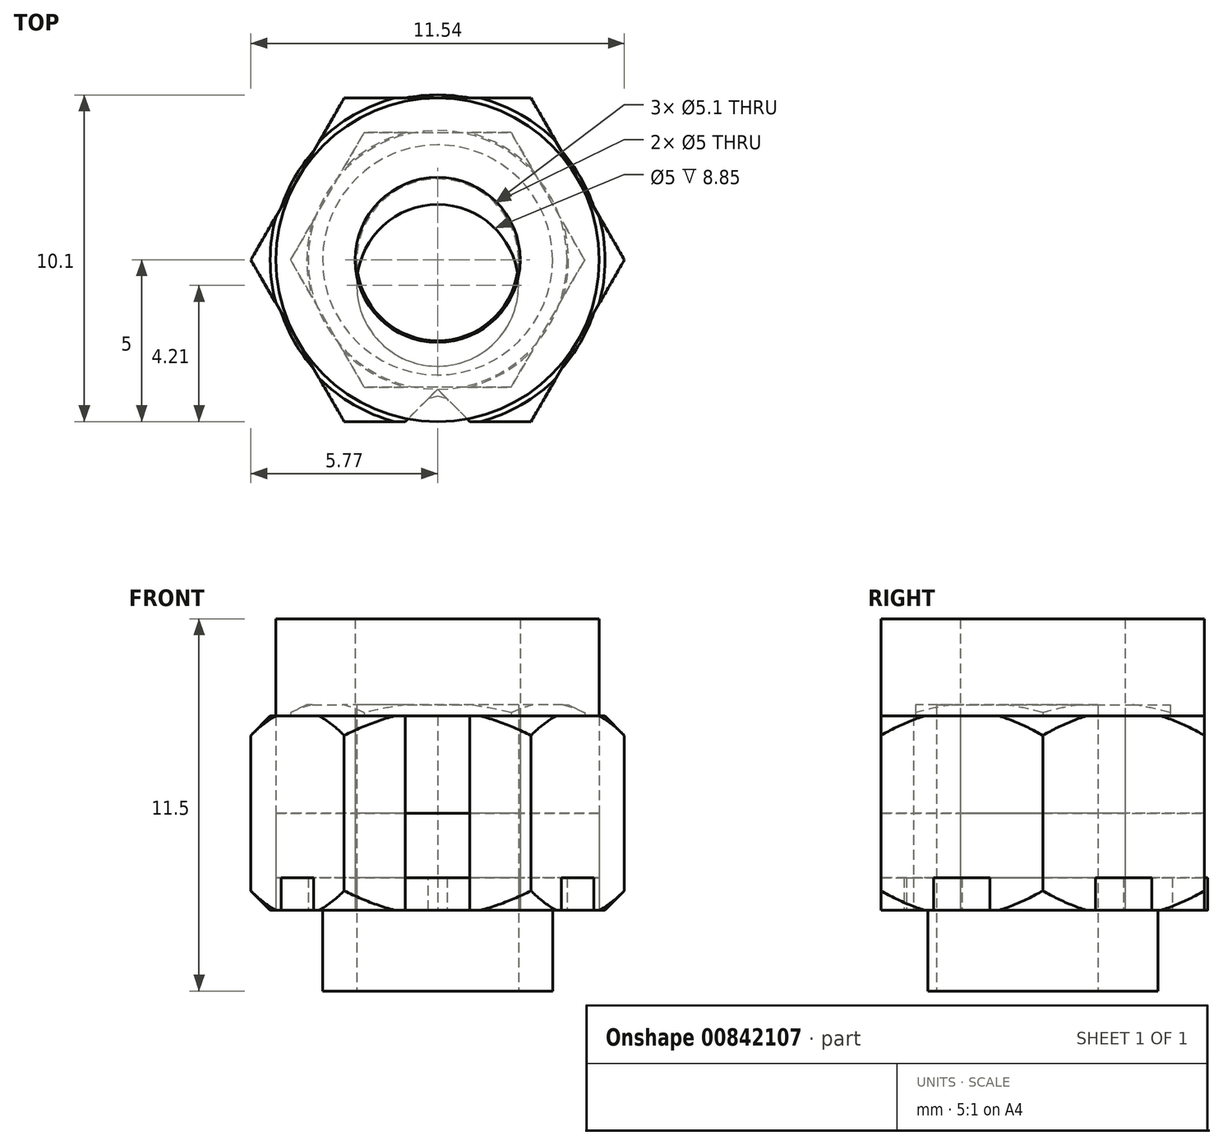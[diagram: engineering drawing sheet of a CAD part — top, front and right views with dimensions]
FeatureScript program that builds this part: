
annotation { "Feature Type Name" : "Feature", "Feature Type Description" : "" }
export const myFeature = defineFeature(function(context is Context, id is Id, definition is map)
    precondition{}
    {
        {
            var Q0;
            Q0=qCreatedBy(makeId("Top.planeOp"),FACE);
            var sketch = newSketch(context, id + "F0", { "sketchPlane" : qUnion([Q0])});
            skArc(sketch, "E0", {"start": v(1.94, -4.72) * mm, "mid": v(0, 5.1) * mm, "end": v(-1.94, -4.72) * mm});
            skCircle(sketch, "E1", {"center": v(0, 0) * mm, "radius": 3.56 * mm});
            skCircle(sketch, "E2", {"center": v(0, -0.79) * mm, "radius": 2.5 * mm});
            skLineSegment(sketch, "E3", {"start": v(-1.94, -4.72) * mm, "end": v(1.94, -4.72) * mm, "construction": true});
            skLineSegment(sketch, "E4", {"start": v(1.94, -4.72) * mm, "end": v(0, -4.22) * mm});
            skLineSegment(sketch, "E5", {"start": v(0, -4.22) * mm, "end": v(-1.94, -4.72) * mm});
            skCircle(sketch, "E6.cCircle", {"center": v(0, 0) * mm, "radius": 3.94 * mm, "construction": true});
            skLineSegment(sketch, "E6.0", {"start": v(-2.27, 3.94) * mm, "end": v(2.27, 3.94) * mm});
            skLineSegment(sketch, "E6.1", {"start": v(2.27, 3.93) * mm, "end": v(4.54, 0) * mm});
            skLineSegment(sketch, "E6.2", {"start": v(4.54, 0) * mm, "end": v(2.27, -3.94) * mm});
            skLineSegment(sketch, "E6.3", {"start": v(2.27, -3.94) * mm, "end": v(-2.27, -3.94) * mm});
            skLineSegment(sketch, "E6.4", {"start": v(-2.27, -3.94) * mm, "end": v(-4.54, 0) * mm});
            skLineSegment(sketch, "E6.5", {"start": v(-4.54, 0) * mm, "end": v(-2.27, 3.94) * mm});
            skPoint(sketch, "E6.0.midPoint", {"position": v(0, 3.94) * mm});
            skSolve(sketch);
        }
        {
            var Q0;
            Q0=makeQuery(id+"F0.imprint","IMPRINT",FACE,{"disambiguationData":[TD([[makeQuery(id+"F0.imprint","IMPRINT",EDGE,{"derivedFrom":sQuery(id+"F0.wireOp",EDGE,"E1")}),-1.0]])]});
            var Q1;
            Q1=makeQuery(id+"F0.imprint","IMPRINT",FACE,{"disambiguationData":[TD([[makeQuery(id+"F0.imprint","IMPRINT",EDGE,{"derivedFrom":sQuery(id+"F0.wireOp",EDGE,"E1")}),1.0]])]});
            extrude(context, id + "F1", {"entities" : qUnion([Q0, Q1]), "depth" : 6.35 * mm, "offsetDistance" : 25 * mm});
        }
        {
            var Q0;
            Q0=makeQuery(id+"F0.imprint","IMPRINT",FACE,{"disambiguationData":[TD([[makeQuery(id+"F0.imprint","IMPRINT",EDGE,{"derivedFrom":sQuery(id+"F0.wireOp",EDGE,"E0")}),1.0]])]});
            extrude(context, id + "F2", {"entities" : qUnion([Q0]), "operationType" : NewBodyOperationType.ADD, "depth" : 1 * mm, "offsetDistance" : 25 * mm});
        }
        {
            var Q0;
            Q0=makeQuery(id+"F0.imprint","IMPRINT",FACE,{"disambiguationData":[TD([[makeQuery(id+"F0.imprint","IMPRINT",EDGE,{"derivedFrom":sQuery(id+"F0.wireOp",EDGE,"E1")}),1.0]])]});
            extrude(context, id + "F3", {"entities" : qUnion([Q0]), "operationType" : NewBodyOperationType.ADD, "oppositeDirection" : true, "depth" : 2.5 * mm, "offsetDistance" : 25 * mm});
        }
        {
            var Q0;
            Q0=qCreatedBy(makeId("Front.planeOp"),FACE);
            var sketch = newSketch(context, id + "F4", { "sketchPlane" : qUnion([Q0])});
            skPoint(sketch, "E7.0", {"position": v(4.54, 6.35) * mm});
            skLineSegment(sketch, "E8", {"start": v(4.54, 6.35) * mm, "end": v(4.54, 6.1) * mm});
            skLineSegment(sketch, "E9", {"start": v(4.54, 6.1) * mm, "end": v(4.04, 6.35) * mm});
            skLineSegment(sketch, "E10", {"start": v(4.04, 6.35) * mm, "end": v(4.54, 6.35) * mm});
            skLineSegment(sketch, "E11", {"start": v(0, 0) * mm, "end": v(0, 6.35) * mm, "construction": true});
            skSolve(sketch);
        }
        {
            var Q0;
            Q0=qSketchRegion(id+"F4",true);
            var Q1;
            Q1=sQuery(id+"F4.wireOp",EDGE,"E11");
            revolve(context, id + "F5", {"operationType" : NewBodyOperationType.REMOVE, "entities" : qUnion([Q0]), "axis" : qUnion([Q1]), "revolveType" : RevolveType.FULL, "oppositeDirection" : true});
        }
        {
            var Q0;
            Q0=qCreatedBy(makeId("Top.planeOp"),FACE);
            var sketch = newSketch(context, id + "F6", { "sketchPlane" : qUnion([Q0])});
            skCircle(sketch, "E12", {"center": v(0, 0) * mm, "radius": 3.56 * mm});
            skCircle(sketch, "E13", {"center": v(0, -0.79) * mm, "radius": 2.5 * mm});
            skCircle(sketch, "E14.cCircle", {"center": v(0, 0) * mm, "radius": 5 * mm, "construction": true});
            skLineSegment(sketch, "E14.0", {"start": v(-2.89, 5) * mm, "end": v(2.89, 5) * mm});
            skLineSegment(sketch, "E14.1", {"start": v(2.89, 5) * mm, "end": v(5.77, 0) * mm});
            skLineSegment(sketch, "E14.2", {"start": v(5.77, 0) * mm, "end": v(2.89, -5) * mm});
            skLineSegment(sketch, "E14.3", {"start": v(2.89, -5) * mm, "end": v(-2.89, -5) * mm});
            skLineSegment(sketch, "E14.4", {"start": v(-2.89, -5) * mm, "end": v(-5.77, 0) * mm});
            skLineSegment(sketch, "E14.5", {"start": v(-5.77, 0) * mm, "end": v(-2.89, 5) * mm});
            skPoint(sketch, "E14.0.midPoint", {"position": v(0, 5) * mm});
            skLineSegment(sketch, "E15", {"start": v(0, -4) * mm, "end": v(-1, -5) * mm});
            skLineSegment(sketch, "E16", {"start": v(1, -5) * mm, "end": v(0, -4) * mm});
            skLineSegment(sketch, "E17", {"start": v(0, 0) * mm, "end": v(0, 1.8) * mm, "construction": true});
            skSolve(sketch);
        }
        {
            var Q0;
            Q0=makeQuery(id+"F6.imprint","IMPRINT",FACE,{"disambiguationData":[TD([[makeQuery(id+"F6.imprint","IMPRINT",EDGE,{"derivedFrom":sQuery(id+"F6.wireOp",EDGE,"E12")}),1.0]])]});
            extrude(context, id + "F7", {"entities" : qUnion([Q0]), "oppositeDirection" : true, "depth" : 2.5 * mm, "offsetDistance" : 25 * mm});
        }
        {
            var Q0;
            Q0=makeQuery(id+"F6.imprint","IMPRINT",FACE,{"disambiguationData":[TD([[makeQuery(id+"F6.imprint","IMPRINT",EDGE,{"derivedFrom":sQuery(id+"F6.wireOp",EDGE,"E12")}),1.0]])]});
            var Q1;
            Q1=makeQuery(id+"F6.imprint","IMPRINT",FACE,{"disambiguationData":[TD([[makeQuery(id+"F6.imprint","IMPRINT",EDGE,{"derivedFrom":sQuery(id+"F6.wireOp",EDGE,"E12")}),-1.0]])]});
            extrude(context, id + "F8", {"entities" : qUnion([Q0, Q1]), "operationType" : NewBodyOperationType.ADD, "depth" : 6 * mm, "offsetDistance" : 25 * mm});
        }
        {
            var Q0;
            Q0=qCreatedBy(makeId("Front.planeOp"),FACE);
            var sketch = newSketch(context, id + "F9", { "sketchPlane" : qUnion([Q0])});
            skPoint(sketch, "E18.0", {"position": v(-5.77, 6) * mm});
            skLineSegment(sketch, "E19", {"start": v(-5.77, 6) * mm, "end": v(-5.77, 5.4) * mm});
            skLineSegment(sketch, "E20", {"start": v(-5.77, 6) * mm, "end": v(-5.17, 6) * mm});
            skLineSegment(sketch, "E21", {"start": v(-5.77, 5.4) * mm, "end": v(-5.17, 6) * mm});
            skLineSegment(sketch, "E22", {"start": v(0, 0) * mm, "end": v(0, 2) * mm, "construction": true});
            skPoint(sketch, "E23.0", {"position": v(-5.77, 3) * mm});
            skLineSegment(sketch, "E24", {"start": v(-5.77, 3) * mm, "end": v(-3.77, 3) * mm, "construction": true});
            skLineSegment(sketch, "E25.MirrorCS", {"start": v(-5.77, 0.6) * mm, "end": v(-5.17, 0) * mm});
            skLineSegment(sketch, "E26.MirrorCS", {"start": v(-5.77, 0) * mm, "end": v(-5.17, 0) * mm});
            skLineSegment(sketch, "E27.MirrorCS", {"start": v(-5.77, 0) * mm, "end": v(-5.77, 0.6) * mm});
            skPoint(sketch, "E28.MirrorP", {"position": v(-5.77, 0) * mm});
            skSolve(sketch);
        }
        {
            var Q0;
            Q0=makeQuery(id+"F9.imprint","IMPRINT",FACE,{"disambiguationData":[TD([[makeQuery(id+"F9.imprint","IMPRINT",EDGE,{"derivedFrom":sQuery(id+"F9.wireOp",EDGE,"E19")}),1.0]])]});
            var Q1;
            Q1=makeQuery(id+"F9.imprint","IMPRINT",FACE,{"disambiguationData":[TD([[makeQuery(id+"F9.imprint","IMPRINT",EDGE,{"derivedFrom":sQuery(id+"F9.wireOp",EDGE,"E25.MirrorCS")}),-1.0]])]});
            var Q2;
            Q2=sQuery(id+"F9.wireOp",EDGE,"E22");
            revolve(context, id + "F10", {"operationType" : NewBodyOperationType.REMOVE, "entities" : qUnion([Q0, Q1]), "axis" : qUnion([Q2]), "revolveType" : RevolveType.FULL, "oppositeDirection" : true});
        }
        {
            var Q0;
            Q0=qCreatedBy(makeId("Top.planeOp"),FACE);
            var sketch = newSketch(context, id + "F11", { "sketchPlane" : qUnion([Q0])});
            skCircle(sketch, "E29", {"center": v(0, 0) * mm, "radius": 2.5 * mm});
            skCircle(sketch, "E30", {"center": v(0, 0) * mm, "radius": 5 * mm});
            skCircle(sketch, "E31", {"center": v(0, 0) * mm, "radius": 4 * mm});
            skSolve(sketch);
        }
        {
            var Q0;
            Q0=qSketchRegion(id+"F11",true);
            var Q1;
            Q1=makeQuery(id+"F11.imprint","IMPRINT",FACE,{"disambiguationData":[TD([[makeQuery(id+"F11.imprint","IMPRINT",EDGE,{"derivedFrom":sQuery(id+"F11.wireOp",EDGE,"E29")}),-1.0]])]});
            extrude(context, id + "F12", {"entities" : qUnion([Q0, Q1]), "depth" : 1 * mm, "offsetDistance" : 25 * mm});
        }
        {
            var Q0;
            Q0=makeQuery(id+"F11.imprint","IMPRINT",FACE,{"disambiguationData":[TD([[makeQuery(id+"F11.imprint","IMPRINT",EDGE,{"derivedFrom":sQuery(id+"F11.wireOp",EDGE,"E29")}),-1.0]])]});
            extrude(context, id + "F13", {"entities" : qUnion([Q0]), "depth" : 1 * mm, "offsetDistance" : 25 * mm});
        }
        {
            var Q0;
            Q0=qCreatedBy(makeId("Top.planeOp"),FACE);
            var sketch = newSketch(context, id + "F14", { "sketchPlane" : qUnion([Q0])});
            skCircle(sketch, "E32", {"center": v(0, 0) * mm, "radius": 5 * mm});
            skCircle(sketch, "E33", {"center": v(0, 0) * mm, "radius": 2.55 * mm});
            skSolve(sketch);
        }
        {
            var Q0;
            Q0=makeQuery(id+"F14.imprint","IMPRINT",FACE,{"disambiguationData":[TD([[makeQuery(id+"F14.imprint","IMPRINT",EDGE,{"derivedFrom":sQuery(id+"F14.wireOp",EDGE,"E32")}),1.0]])]});
            extrude(context, id + "F15", {"entities" : qUnion([Q0]), "depth" : 6 * mm, "offsetDistance" : 25 * mm});
        }
        {
            var Q0;
            Q0=makeQuery(id+"F14.imprint","IMPRINT",FACE,{"disambiguationData":[TD([[makeQuery(id+"F14.imprint","IMPRINT",EDGE,{"derivedFrom":sQuery(id+"F14.wireOp",EDGE,"E32")}),1.0]])]});
            extrude(context, id + "F16", {"entities" : qUnion([Q0]), "depth" : 3 * mm, "offsetDistance" : 25 * mm});
        }
        {
            var Q0;
            Q0=makeQuery(id+"F14.imprint","IMPRINT",FACE,{"disambiguationData":[TD([[makeQuery(id+"F14.imprint","IMPRINT",EDGE,{"derivedFrom":sQuery(id+"F14.wireOp",EDGE,"E32")}),1.0]])]});
            extrude(context, id + "F17", {"entities" : qUnion([Q0]), "depth" : 9 * mm, "offsetDistance" : 25 * mm});
        }
    });
